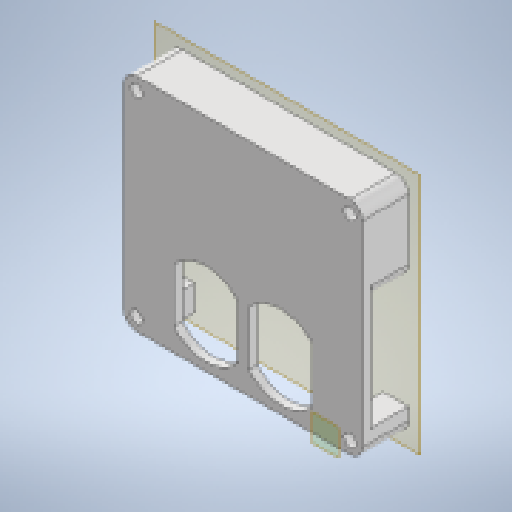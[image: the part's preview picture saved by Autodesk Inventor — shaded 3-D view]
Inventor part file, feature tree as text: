
AUTODESK INVENTOR PART (.ipt)
format: ipt  version: 2023 (Build 270158000, 158)  size: 281,600 bytes
history: native  units: mm
features: other x7, reference x4, plane x3, extrude x3, sketch x1, fillet x1
ambient origin geometry x8: Origin, YZ Plane, XZ Plane, XY Plane, X Axis, Y Axis, Z Axis, Center Point
bodies: Solid1 (feature_tree)
feature tree (19):
  plane  "Work Plane1"
  plane  "Work Plane2"
  plane  "Work Plane3"
  extrude  "Extrusion1"  TaperAngle=0.0deg  [1 undecoded]
  sketch  "Sketch4"  dims[d10=9.0mm d11=0.0mm d56=0.0mm d68=3.0mm d69=3.0mm d70=20.0mm d72=51.188mm d73=20.0mm d75=47.043mm d84=5.0mm d88=2.0mm d89=0.0mm d90=2.0mm d91=0.0mm d92=3.0mm d93=0.1mm d94=0.5mm d96=0.5mm d97=0.1mm d98=0.1mm d99=0.0mm d100=0.5mm d101=0.872665mm d102=0.5mm d103=0.872665mm]
  extrude  "Extrusion6"  Depth=3.0mm
  extrude  "Extrusion7"  Depth=3.0mm
  fillet  "Fillet2"  Radius=51.188mm
  reference  "Reference27"
  reference  "Reference28"
  reference  "Reference29"
  reference  "Reference30"
  parser-record x1  (decoder bookkeeping rows leaked as tree rows — omitted from the tree; the rows remain in map.json)
  other  "Assembly_V6.iam"
  other  "rack_V6:1"
  other  "motor:2"
  other  "motor:1"
  other  "mouldingPlate_V6:1"
  other  "screw:1"
note: 1 required parameter value undecoded (feature->parameter linkage not recoverable at this tier; creation-order binding heuristic only, values carry confidence <= 0.55)
note: 1 file-system path scrubbed to <path> (originals preserved in map.json)
